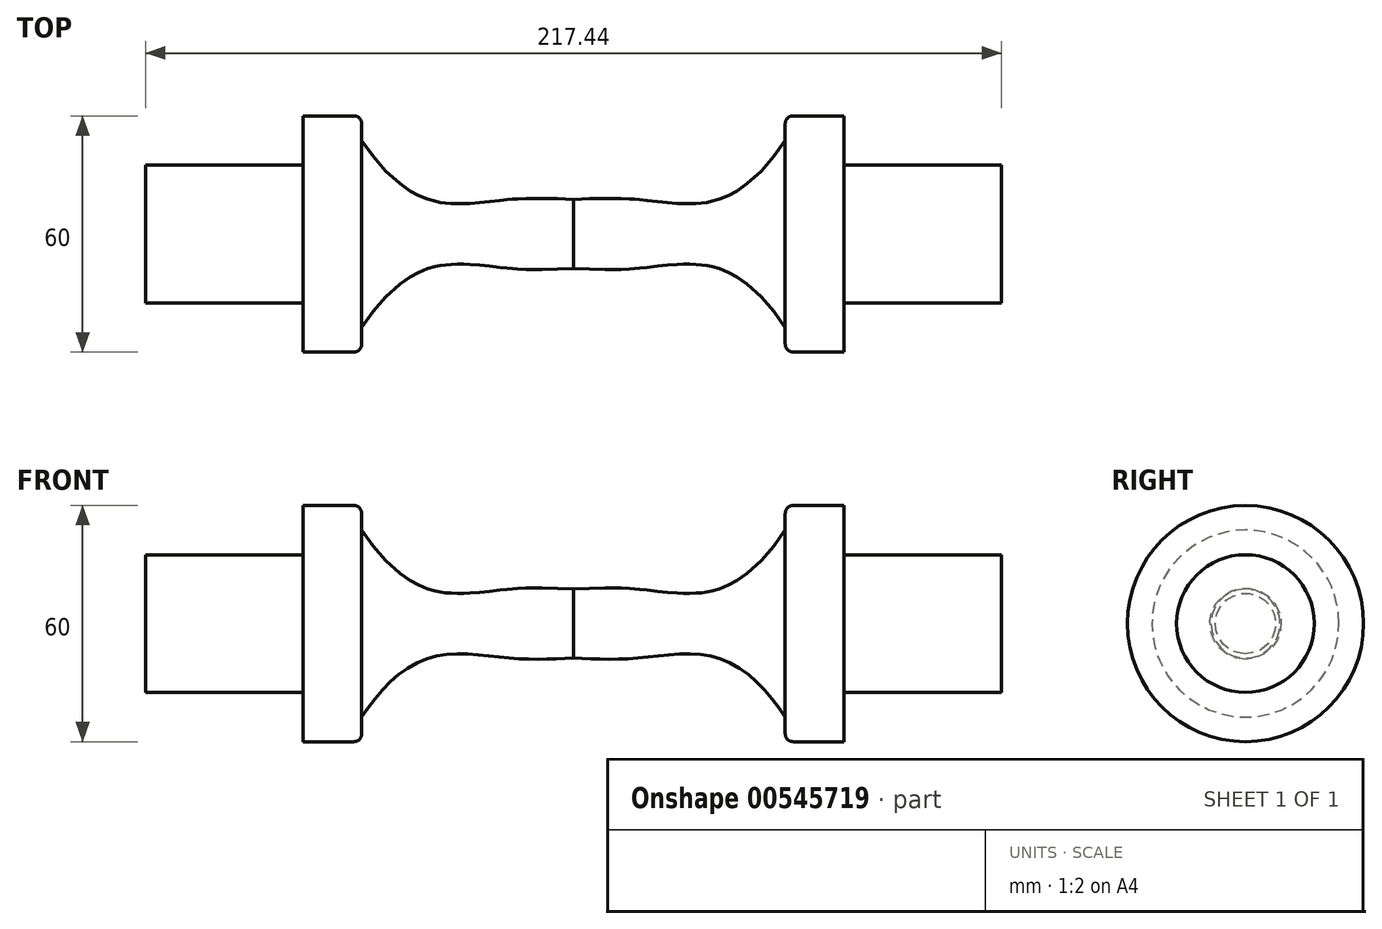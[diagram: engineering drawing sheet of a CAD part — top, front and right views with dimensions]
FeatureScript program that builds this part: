
annotation { "Feature Type Name" : "Feature", "Feature Type Description" : "" }
export const myFeature = defineFeature(function(context is Context, id is Id, definition is map)
    precondition{}
    {
        {
            var Q0;
            Q0=qCreatedBy(makeId("Front.planeOp"),FACE);
            var sketch = newSketch(context, id + "F0", { "sketchPlane" : qUnion([Q0])});
            skLineSegment(sketch, "E0", {"start": v(0, 0) * mm, "end": v(0, 17.5) * mm});
            skLineSegment(sketch, "E1", {"start": v(53.8, 23.75) * mm, "end": v(53.8, 28) * mm});
            skLineSegment(sketch, "E2", {"start": v(55.8, 30) * mm, "end": v(68.72, 30) * mm});
            skLineSegment(sketch, "E3", {"start": v(68.72, 30) * mm, "end": v(68.72, 17.5) * mm});
            skLineSegment(sketch, "E4", {"start": v(68.72, 17.5) * mm, "end": v(108.72, 17.5) * mm});
            skLineSegment(sketch, "E5", {"start": v(108.72, 17.5) * mm, "end": v(108.72, 0) * mm});
            skLineSegment(sketch, "E6", {"start": v(108.72, 0) * mm, "end": v(0, 0) * mm});
            skPoint(sketch, "E7.1.internal.snap0", {"position": v(0, 8.75) * mm});
            skPoint(sketch, "E7.0.internal.orphan", {"position": v(0, 8.75) * mm});
            skPoint(sketch, "E7.1.internal.orphan", {"position": v(16.26, 8.75) * mm});
            skFitSpline(sketch, "E8", {"points": [v(0, 8.75) * mm, v(16.26, 8.75) * mm, v(36.81, 8.75) * mm, v(53.8, 23.75) * mm], "startDerivative": vector(49.97, 2.73) * mm, "endDerivative": vector(34.9, 54.98) * mm});
            skPoint(sketch, "E9.orphan", {"position": v(53.8, 17.5) * mm});
            skPoint(sketch, "E10.visualSharp", {"position": v(53.8, 30) * mm});
            skArc(sketch, "E10.filletArc", {"start": v(55.8, 30) * mm, "mid": v(54.38, 29.41) * mm, "end": v(53.8, 28) * mm});
            skSolve(sketch);
        }
        {
            var Q0;
            Q0 = qSketchRegion(id + "F0", true);
            var Q1;
            Q1=sQuery(id+"F0.wireOp",EDGE,"E6");
            revolve(context, id + "F1", {"entities" : qUnion([Q0]), "axis" : qUnion([Q1]), "revolveType" : RevolveType.FULL});
        }
        {
            var Q0;
            Q0=makeQuery(id+"F1.opRevolve","SWEPT_BODY",BODY,{"disambiguationData":[OSD([sQuery(id+"F0.wireOp",EDGE,"E0"),sQuery(id+"F0.wireOp",EDGE,"E1"),sQuery(id+"F0.wireOp",EDGE,"E2"),sQuery(id+"F0.wireOp",EDGE,"E3"),sQuery(id+"F0.wireOp",EDGE,"E4"),sQuery(id+"F0.wireOp",EDGE,"E5"),sQuery(id+"F0.wireOp",EDGE,"E6"),sQuery(id+"F0.wireOp",EDGE,"E8"),sQuery(id+"F0.wireOp",EDGE,"E10.filletArc")])]});
            var Q1;
            Q1=makeQuery(id+"F1.opRevolve","SWEPT_FACE",FACE,{"disambiguationData":[OSD([sQuery(id+"F0.wireOp",EDGE,"E0")])]});
            mirror(context, id + "F2", {"operationType" : NewBodyOperationType.ADD, "entities" : qUnion([Q0]), "mirrorPlane" : qUnion([Q1])});
        }
    });
